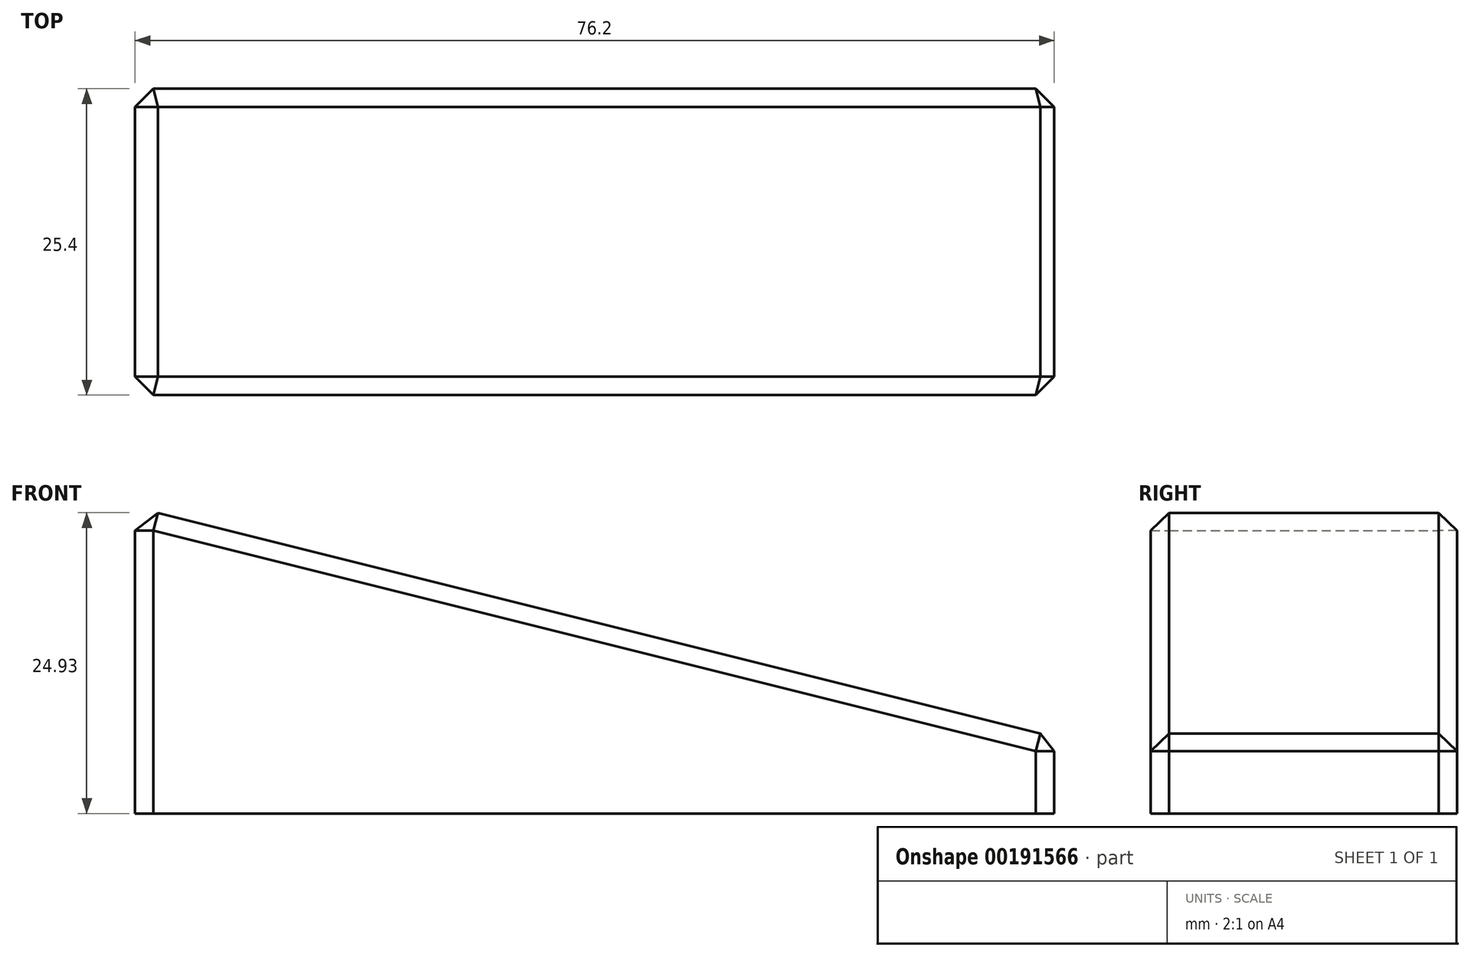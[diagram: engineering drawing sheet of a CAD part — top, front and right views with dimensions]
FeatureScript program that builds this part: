
annotation { "Feature Type Name" : "Feature", "Feature Type Description" : "" }
export const myFeature = defineFeature(function(context is Context, id is Id, definition is map)
    precondition{}
    {
        {
            var Q0;
            Q0=qCreatedBy(makeId("Front.planeOp"),FACE);
            var sketch = newSketch(context, id + "F0", { "sketchPlane" : qUnion([Q0])});
            skLineSegment(sketch, "E0", {"start": v(0, 0) * mm, "end": v(38.1, 0) * mm});
            skLineSegment(sketch, "E1", {"start": v(0, 0) * mm, "end": v(-38.1, 0) * mm});
            skLineSegment(sketch, "E2", {"start": v(-38.1, 0) * mm, "end": v(-38.1, 25.4) * mm});
            skLineSegment(sketch, "E3", {"start": v(38.1, 0) * mm, "end": v(38.1, 6.35) * mm});
            skLineSegment(sketch, "E4", {"start": v(38.1, 6.35) * mm, "end": v(-38.1, 25.4) * mm});
            skSolve(sketch);
        }
        {
            var Q0;
            Q0 = qSketchRegion(id + "F0", true);
            extrude(context, id + "F1", {"entities" : qUnion([Q0]), "endBound" : BoundingType.SYMMETRIC, "depth" : 25.4 * mm});
        }
        {
            var Q0;
            Q0=makeQuery(id+"F1.opExtrude","SWEPT_EDGE",EDGE,{"disambiguationData":[OSD([sQuery(id+"F0.wireOp",EDGE,"E2"),sQuery(id+"F0.wireOp",EDGE,"E4")])]});
            var Q1;
            Q1=makeQuery(id+"F1.opExtrude","CAP_EDGE",EDGE,{"disambiguationData":[OSD([sQuery(id+"F0.wireOp",EDGE,"E4")])],"isStart":true});
            var Q2;
            Q2=makeQuery(id+"F1.opExtrude","CAP_EDGE",EDGE,{"disambiguationData":[OSD([sQuery(id+"F0.wireOp",EDGE,"E4")])],"isStart":false});
            var Q3;
            Q3=makeQuery(id+"F1.opExtrude","SWEPT_EDGE",EDGE,{"disambiguationData":[OSD([sQuery(id+"F0.wireOp",EDGE,"E3"),sQuery(id+"F0.wireOp",EDGE,"E4")])]});
            var Q4;
            Q4=makeQuery(id+"F1.opExtrude","CAP_EDGE",EDGE,{"disambiguationData":[OSD([sQuery(id+"F0.wireOp",EDGE,"E2")])],"isStart":false});
            var Q5;
            Q5=makeQuery(id+"F1.opExtrude","CAP_EDGE",EDGE,{"disambiguationData":[OSD([sQuery(id+"F0.wireOp",EDGE,"E2")])],"isStart":true});
            var Q6;
            Q6=makeQuery(id+"F1.opExtrude","CAP_EDGE",EDGE,{"disambiguationData":[OSD([sQuery(id+"F0.wireOp",EDGE,"E3")])],"isStart":false});
            var Q7;
            Q7=makeQuery(id+"F1.opExtrude","CAP_EDGE",EDGE,{"disambiguationData":[OSD([sQuery(id+"F0.wireOp",EDGE,"E3")])],"isStart":true});
            chamfer(context, id + "F2", {"entities" : qUnion([Q0, Q1, Q2, Q3, Q4, Q5, Q6, Q7]), "width" : 1.52 * mm, "tangentPropagation" : true});
        }
    });
